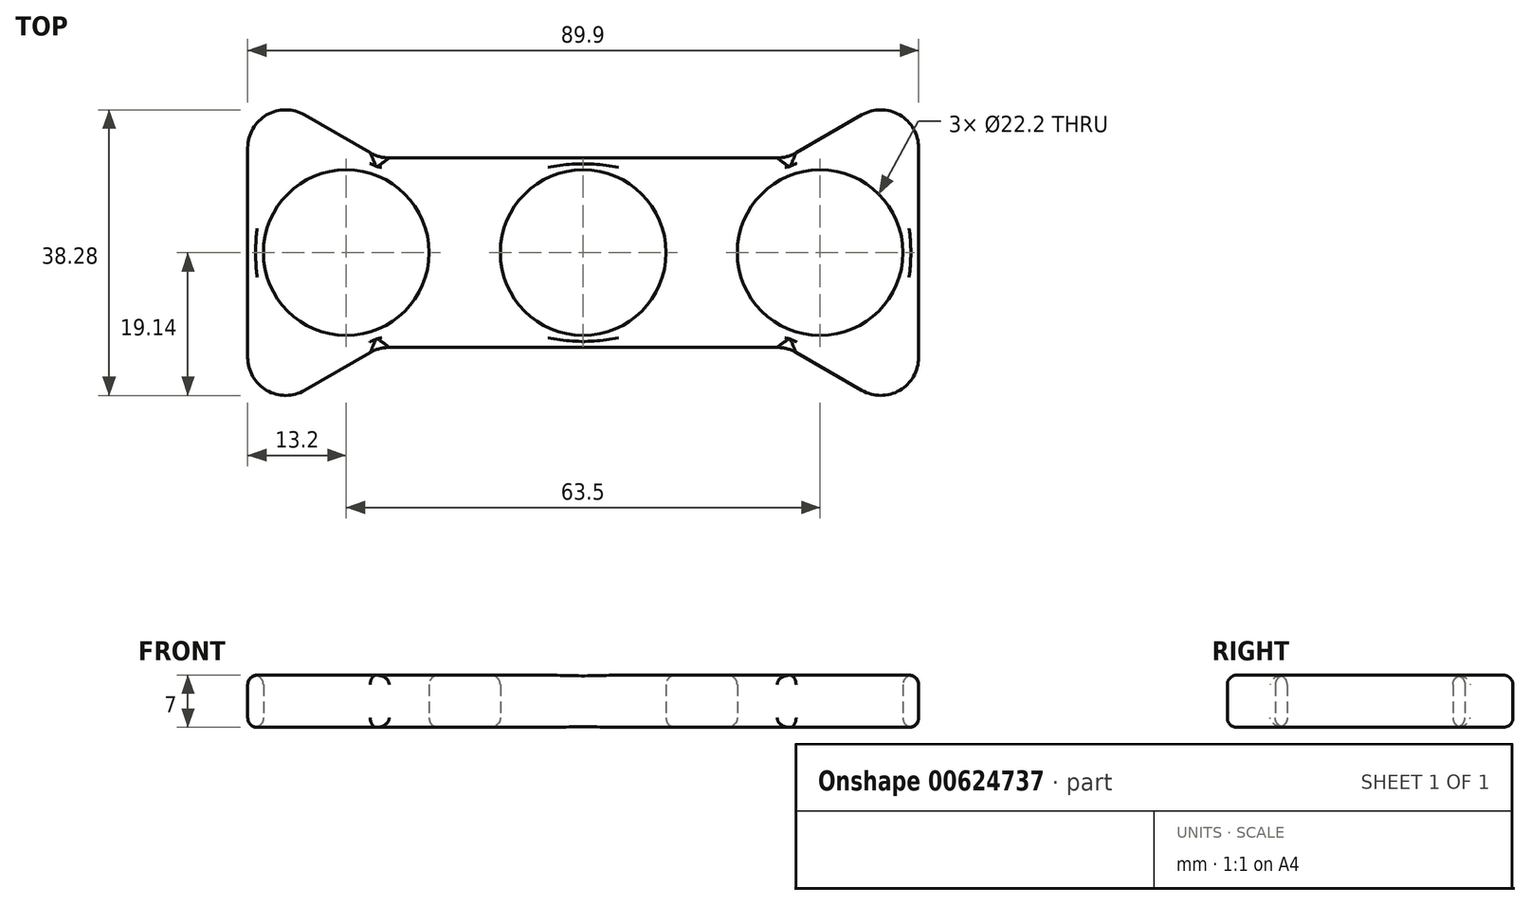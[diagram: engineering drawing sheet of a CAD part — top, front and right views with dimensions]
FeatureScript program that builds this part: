
annotation { "Feature Type Name" : "Feature", "Feature Type Description" : "" }
export const myFeature = defineFeature(function(context is Context, id is Id, definition is map)
    precondition{}
    {
        {
            var Q0;
            Q0=qCreatedBy(makeId("Top.planeOp"),FACE);
            var sketch = newSketch(context, id + "F0", { "sketchPlane" : qUnion([Q0])});
            skLineSegment(sketch, "E0.bottom", {"start": v(-31.75, 12.7) * mm, "end": v(31.75, 12.7) * mm});
            skLineSegment(sketch, "E0.top", {"start": v(-31.75, -12.7) * mm, "end": v(31.75, -12.7) * mm});
            skLineSegment(sketch, "E0.left", {"start": v(-31.75, 12.7) * mm, "end": v(-31.75, -12.7) * mm});
            skLineSegment(sketch, "E0.right", {"start": v(31.75, 12.7) * mm, "end": v(31.75, -12.7) * mm});
            skPoint(sketch, "E0.middle", {"position": v(0, 0) * mm});
            skCircle(sketch, "E1", {"center": v(0, 0) * mm, "radius": 11.1 * mm});
            skCircle(sketch, "E2", {"center": v(-31.75, 0) * mm, "radius": 11.1 * mm});
            skCircle(sketch, "E3", {"center": v(31.75, 0) * mm, "radius": 11.1 * mm});
            skCircle(sketch, "E4.cCircle", {"center": v(-31.75, 0) * mm, "radius": 13.2 * mm, "construction": true});
            skLineSegment(sketch, "E4.0", {"start": v(-44.95, -22.86) * mm, "end": v(-44.95, 22.86) * mm});
            skLineSegment(sketch, "E4.1", {"start": v(-44.95, 22.86) * mm, "end": v(-5.35, 0) * mm});
            skLineSegment(sketch, "E4.2", {"start": v(-5.35, 0) * mm, "end": v(-44.95, -22.86) * mm});
            skPoint(sketch, "E4.0.midPoint", {"position": v(-44.95, 0) * mm});
            skCircle(sketch, "E5.cCircle", {"center": v(31.75, 0) * mm, "radius": 13.2 * mm, "construction": true});
            skLineSegment(sketch, "E5.0", {"start": v(44.95, 22.86) * mm, "end": v(44.95, -22.86) * mm});
            skLineSegment(sketch, "E5.1", {"start": v(44.95, -22.86) * mm, "end": v(5.35, 0) * mm});
            skLineSegment(sketch, "E5.2", {"start": v(5.35, 0) * mm, "end": v(44.95, 22.86) * mm});
            skPoint(sketch, "E5.0.midPoint", {"position": v(44.95, 0) * mm});
            skSolve(sketch);
        }
        {
            var Q0;
            Q0 = qSketchRegion(id + "F0", true);
            extrude(context, id + "F1", {"entities" : qUnion([Q0]), "depth" : 7 * mm, "offsetDistance" : 25.4 * mm});
        }
        {
            var Q0;
            Q0=makeQuery(id+"F1.opExtrude","CAP_EDGE",EDGE,{"disambiguationData":[OSD([sQuery(id+"F0.wireOp",EDGE,"E0.bottom")])],"isStart":false});
            var Q1;
            Q1=makeQuery(id+"F1.opExtrude","CAP_EDGE",EDGE,{"disambiguationData":[OSD([sQuery(id+"F0.wireOp",EDGE,"E0.top")])],"isStart":false});
            var Q2;
            Q2=makeQuery(id+"F1.opExtrude","CAP_EDGE",EDGE,{"disambiguationData":[OSD([sQuery(id+"F0.wireOp",EDGE,"E1")])],"isStart":false});
            var Q3;
            Q3=makeQuery(id+"F1.opExtrude","CAP_EDGE",EDGE,{"disambiguationData":[OSD([sQuery(id+"F0.wireOp",EDGE,"E3")])],"isStart":false});
            var Q4;
            Q4=makeQuery(id+"F1.opExtrude","CAP_EDGE",EDGE,{"disambiguationData":[OSD([sQuery(id+"F0.wireOp",EDGE,"E2")])],"isStart":false});
            var Q5;
            Q5=makeQuery(id+"F1.opExtrude","CAP_EDGE",EDGE,{"disambiguationData":[OSD([sQuery(id+"F0.wireOp",EDGE,"E4.2")])],"isStart":false});
            var Q6;
            Q6=makeQuery(id+"F1.opExtrude","CAP_EDGE",EDGE,{"disambiguationData":[OSD([sQuery(id+"F0.wireOp",EDGE,"E4.0")])],"isStart":false});
            var Q7;
            Q7=makeQuery(id+"F1.opExtrude","CAP_EDGE",EDGE,{"disambiguationData":[OSD([sQuery(id+"F0.wireOp",EDGE,"E4.1")])],"isStart":false});
            var Q8;
            Q8=makeQuery(id+"F1.opExtrude","CAP_EDGE",EDGE,{"disambiguationData":[OSD([sQuery(id+"F0.wireOp",EDGE,"E5.2")])],"isStart":false});
            var Q9;
            Q9=makeQuery(id+"F1.opExtrude","CAP_EDGE",EDGE,{"disambiguationData":[OSD([sQuery(id+"F0.wireOp",EDGE,"E5.0")])],"isStart":false});
            var Q10;
            Q10=makeQuery(id+"F1.opExtrude","CAP_EDGE",EDGE,{"disambiguationData":[OSD([sQuery(id+"F0.wireOp",EDGE,"E5.1")])],"isStart":false});
            fillet(context, id + "F2", {"entities" : qUnion([Q0, Q1, Q2, Q3, Q4, Q5, Q6, Q7, Q8, Q9, Q10]), "radius" : 1.27 * mm, "tangentPropagation" : true, "allowEdgeOverflow" : false});
        }
        {
            var Q0;
            Q0=makeQuery(id+"F1.opExtrude","CAP_EDGE",EDGE,{"disambiguationData":[OSD([sQuery(id+"F0.wireOp",EDGE,"E0.top")])],"isStart":true});
            var Q1;
            Q1=makeQuery(id+"F1.opExtrude","CAP_EDGE",EDGE,{"disambiguationData":[OSD([sQuery(id+"F0.wireOp",EDGE,"E4.2")])],"isStart":true});
            var Q2;
            Q2=makeQuery(id+"F1.opExtrude","CAP_EDGE",EDGE,{"disambiguationData":[OSD([sQuery(id+"F0.wireOp",EDGE,"E4.0")])],"isStart":true});
            var Q3;
            Q3=makeQuery(id+"F1.opExtrude","CAP_EDGE",EDGE,{"disambiguationData":[OSD([sQuery(id+"F0.wireOp",EDGE,"E0.bottom")])],"isStart":true});
            var Q4;
            Q4=makeQuery(id+"F1.opExtrude","CAP_EDGE",EDGE,{"disambiguationData":[OSD([sQuery(id+"F0.wireOp",EDGE,"E4.1")])],"isStart":true});
            var Q5;
            Q5=makeQuery(id+"F1.opExtrude","CAP_EDGE",EDGE,{"disambiguationData":[OSD([sQuery(id+"F0.wireOp",EDGE,"E5.1")])],"isStart":true});
            var Q6;
            Q6=makeQuery(id+"F1.opExtrude","CAP_EDGE",EDGE,{"disambiguationData":[OSD([sQuery(id+"F0.wireOp",EDGE,"E3")])],"isStart":true});
            var Q7;
            Q7=makeQuery(id+"F1.opExtrude","CAP_EDGE",EDGE,{"disambiguationData":[OSD([sQuery(id+"F0.wireOp",EDGE,"E1")])],"isStart":true});
            var Q8;
            Q8=makeQuery(id+"F1.opExtrude","CAP_EDGE",EDGE,{"disambiguationData":[OSD([sQuery(id+"F0.wireOp",EDGE,"E2")])],"isStart":true});
            var Q9;
            Q9=makeQuery(id+"F1.opExtrude","CAP_EDGE",EDGE,{"disambiguationData":[OSD([sQuery(id+"F0.wireOp",EDGE,"E5.2")])],"isStart":true});
            var Q10;
            Q10=makeQuery(id+"F1.opExtrude","CAP_EDGE",EDGE,{"disambiguationData":[OSD([sQuery(id+"F0.wireOp",EDGE,"E5.0")])],"isStart":true});
            fillet(context, id + "F3", {"entities" : qUnion([Q0, Q1, Q2, Q3, Q4, Q5, Q6, Q7, Q8, Q9, Q10]), "radius" : 1.27 * mm, "tangentPropagation" : true, "allowEdgeOverflow" : false});
        }
        {
            var Q0;
            Q0=makeQuery(id+"F1.opExtrude","SWEPT_EDGE",EDGE,{"disambiguationData":[OSD([sQuery(id+"F0.wireOp",EDGE,"E4.0"),sQuery(id+"F0.wireOp",EDGE,"E4.1")])]});
            var Q1;
            Q1=makeQuery(id+"F1.opExtrude","SWEPT_EDGE",EDGE,{"disambiguationData":[OSD([sQuery(id+"F0.wireOp",EDGE,"E5.0"),sQuery(id+"F0.wireOp",EDGE,"E5.2")])]});
            var Q2;
            Q2=makeQuery(id+"F1.opExtrude","SWEPT_EDGE",EDGE,{"disambiguationData":[OSD([sQuery(id+"F0.wireOp",EDGE,"E5.0"),sQuery(id+"F0.wireOp",EDGE,"E5.1")])]});
            var Q3;
            Q3=makeQuery(id+"F1.opExtrude","SWEPT_EDGE",EDGE,{"disambiguationData":[OSD([sQuery(id+"F0.wireOp",EDGE,"E4.0"),sQuery(id+"F0.wireOp",EDGE,"E4.2")])]});
            fillet(context, id + "F4", {"entities" : qUnion([Q0, Q1, Q2, Q3]), "radius" : 5.08 * mm, "tangentPropagation" : true, "allowEdgeOverflow" : false});
        }
        {
            var Q0;
            Q0=makeQuery(id+"F1.opExtrude","SWEPT_EDGE",EDGE,{"disambiguationData":[OSD([sQuery(id+"F0.wireOp",EDGE,"E0.top"),sQuery(id+"F0.wireOp",EDGE,"E5.1")])]});
            var Q1;
            Q1=makeQuery(id+"F1.opExtrude","SWEPT_EDGE",EDGE,{"disambiguationData":[OSD([sQuery(id+"F0.wireOp",EDGE,"E0.top"),sQuery(id+"F0.wireOp",EDGE,"E4.2")])]});
            var Q2;
            Q2=makeQuery(id+"F1.opExtrude","SWEPT_EDGE",EDGE,{"disambiguationData":[OSD([sQuery(id+"F0.wireOp",EDGE,"E0.bottom"),sQuery(id+"F0.wireOp",EDGE,"E4.1")])]});
            var Q3;
            Q3=makeQuery(id+"F1.opExtrude","SWEPT_EDGE",EDGE,{"disambiguationData":[OSD([sQuery(id+"F0.wireOp",EDGE,"E0.bottom"),sQuery(id+"F0.wireOp",EDGE,"E5.2")])]});
            fillet(context, id + "F5", {"entities" : qUnion([Q0, Q1, Q2, Q3]), "radius" : 5.08 * mm, "tangentPropagation" : true, "allowEdgeOverflow" : false});
        }
    });
